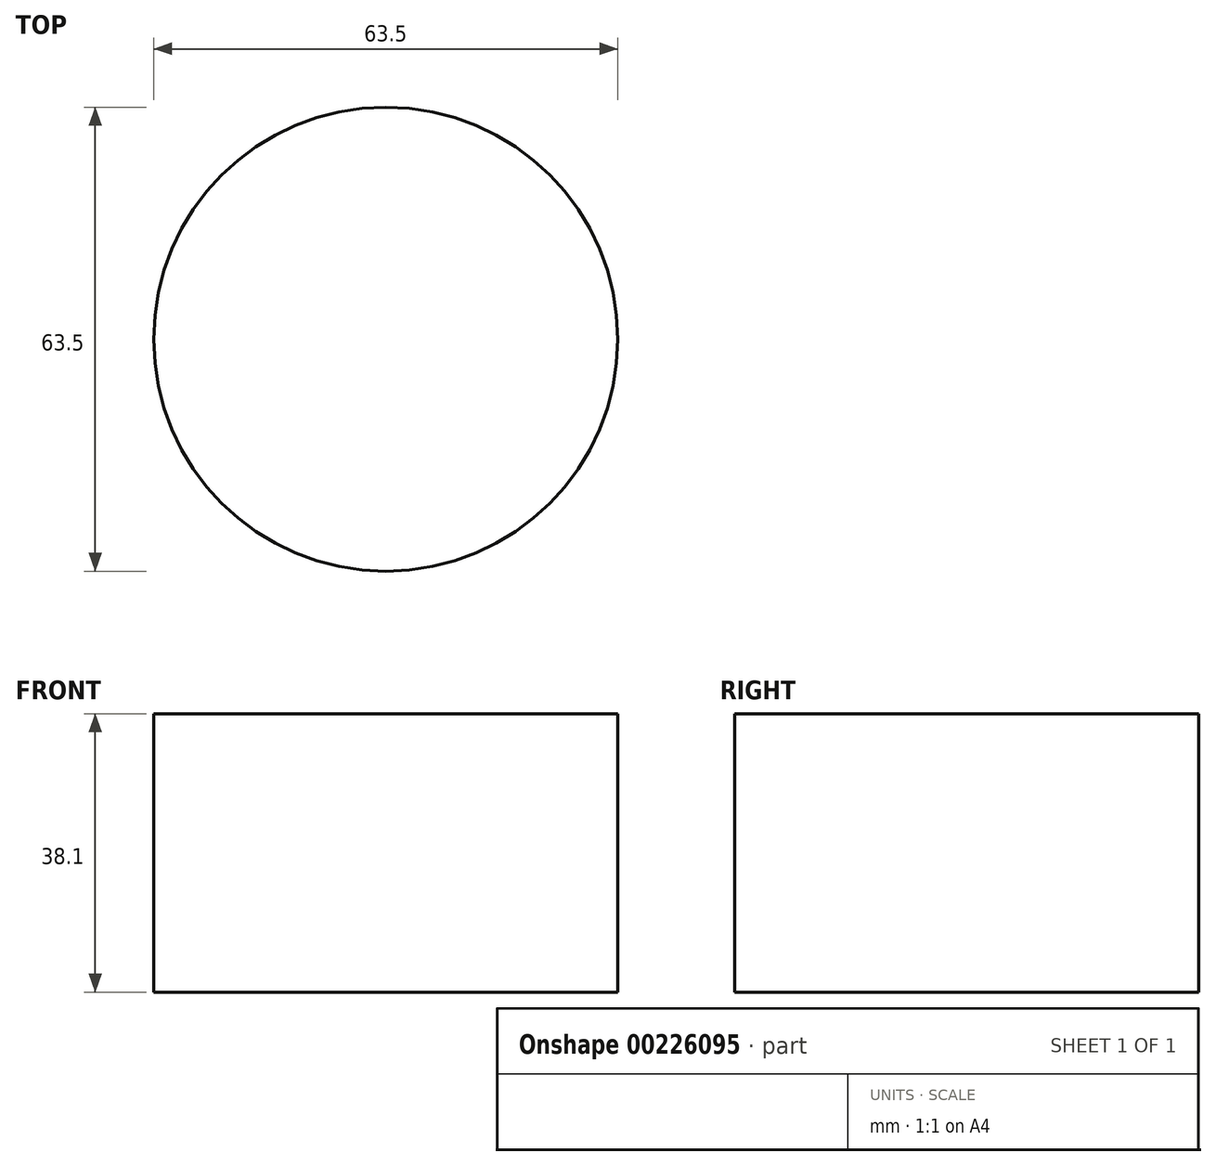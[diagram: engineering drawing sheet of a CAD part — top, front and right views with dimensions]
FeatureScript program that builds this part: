
annotation { "Feature Type Name" : "Feature", "Feature Type Description" : "" }
export const myFeature = defineFeature(function(context is Context, id is Id, definition is map)
    precondition{}
    {
        {
            var Q0;
            Q0=qCreatedBy(makeId("Top.planeOp"),FACE);
            var sketch = newSketch(context, id + "F0", { "sketchPlane" : qUnion([Q0])});
            skCircle(sketch, "E0", {"center": v(0, 0) * mm, "radius": 31.75 * mm});
            skSolve(sketch);
        }
        {
            var Q0;
            Q0=qSketchRegion(id+"F0",true);
            extrude(context, id + "F1", {"entities" : qUnion([Q0]), "depth" : 38.1 * mm});
        }
        {
            var Q0;
            Q0=qCreatedBy(makeId("Top.planeOp"),FACE);
            var sketch = newSketch(context, id + "F2", { "sketchPlane" : qUnion([Q0])});
            skCircle(sketch, "E1", {"center": v(0, 31.75) * mm, "radius": 5.08 * mm});
            skCircle(sketch, "E2.1.0", {"center": v(-18.66, 25.69) * mm, "radius": 5.08 * mm});
            skCircle(sketch, "E2.2.0", {"center": v(-30.2, 9.81) * mm, "radius": 5.08 * mm});
            skCircle(sketch, "E2.3.0", {"center": v(-30.2, -9.81) * mm, "radius": 5.08 * mm});
            skCircle(sketch, "E2.4.0", {"center": v(-18.66, -25.69) * mm, "radius": 5.08 * mm});
            skCircle(sketch, "E2.5.0", {"center": v(0, -31.75) * mm, "radius": 5.08 * mm});
            skCircle(sketch, "E2.6.0", {"center": v(18.66, -25.69) * mm, "radius": 5.08 * mm});
            skCircle(sketch, "E2.7.0", {"center": v(30.2, -9.81) * mm, "radius": 5.08 * mm});
            skCircle(sketch, "E2.8.0", {"center": v(30.2, 9.81) * mm, "radius": 5.08 * mm});
            skCircle(sketch, "E2.9.0", {"center": v(18.66, 25.69) * mm, "radius": 5.08 * mm});
            skPoint(sketch, "E2.center", {"position": v(0, 0) * mm});
            skSolve(sketch);
        }
        {
            var Q0;
            Q0=qSketchRegion(id+"F2",true);
            extrude(context, id + "F3", {"entities" : qUnion([Q0]), "depth" : 50.8 * mm});
        }
        {
            var Q0;
            Q0=makeQuery(id+"F1.opExtrude","SWEPT_BODY",BODY,{"disambiguationData":[OSD([sQuery(id+"F0.wireOp",EDGE,"E0")])]});
            var Q1;
            Q1=makeQuery(id+"F3.opExtrude","SWEPT_BODY",BODY,{"disambiguationData":[OSD([sQuery(id+"F2.wireOp",EDGE,"E1")])]});
            var Q2;
            Q2=makeQuery(id+"F3.opExtrude","SWEPT_BODY",BODY,{"disambiguationData":[OSD([sQuery(id+"F2.wireOp",EDGE,"E2.1.0")])]});
            var Q3;
            Q3=makeQuery(id+"F3.opExtrude","SWEPT_BODY",BODY,{"disambiguationData":[OSD([sQuery(id+"F2.wireOp",EDGE,"E2.2.0")])]});
            var Q4;
            Q4=makeQuery(id+"F3.opExtrude","SWEPT_BODY",BODY,{"disambiguationData":[OSD([sQuery(id+"F2.wireOp",EDGE,"E2.3.0")])]});
            var Q5;
            Q5=makeQuery(id+"F3.opExtrude","SWEPT_BODY",BODY,{"disambiguationData":[OSD([sQuery(id+"F2.wireOp",EDGE,"E2.4.0")])]});
            var Q6;
            Q6=makeQuery(id+"F3.opExtrude","SWEPT_BODY",BODY,{"disambiguationData":[OSD([sQuery(id+"F2.wireOp",EDGE,"E2.5.0")])]});
            var Q7;
            Q7=makeQuery(id+"F3.opExtrude","SWEPT_BODY",BODY,{"disambiguationData":[OSD([sQuery(id+"F2.wireOp",EDGE,"E2.6.0")])]});
            var Q8;
            Q8=makeQuery(id+"F3.opExtrude","SWEPT_BODY",BODY,{"disambiguationData":[OSD([sQuery(id+"F2.wireOp",EDGE,"E2.7.0")])]});
            var Q9;
            Q9=makeQuery(id+"F3.opExtrude","SWEPT_BODY",BODY,{"disambiguationData":[OSD([sQuery(id+"F2.wireOp",EDGE,"E2.8.0")])]});
            var Q10;
            Q10=makeQuery(id+"F3.opExtrude","SWEPT_BODY",BODY,{"disambiguationData":[OSD([sQuery(id+"F2.wireOp",EDGE,"E2.9.0")])]});
            booleanBodies(context, id + "F4", {"operationType" : BooleanOperationType.INTERSECTION, "tools" : qUnion([Q0, Q1, Q2, Q3, Q4, Q5, Q6, Q7, Q8, Q9, Q10]), "keepTools" : true});
        }
        {
            var Q0;
            Q0=makeQuery(id+"F3.opExtrude","SWEPT_BODY",BODY,{"disambiguationData":[OSD([sQuery(id+"F2.wireOp",EDGE,"E2.4.0")])]});
            var Q1;
            Q1=makeQuery(id+"F3.opExtrude","SWEPT_BODY",BODY,{"disambiguationData":[OSD([sQuery(id+"F2.wireOp",EDGE,"E2.3.0")])]});
            var Q2;
            Q2=makeQuery(id+"F3.opExtrude","SWEPT_BODY",BODY,{"disambiguationData":[OSD([sQuery(id+"F2.wireOp",EDGE,"E2.2.0")])]});
            var Q3;
            Q3=makeQuery(id+"F3.opExtrude","SWEPT_BODY",BODY,{"disambiguationData":[OSD([sQuery(id+"F2.wireOp",EDGE,"E2.1.0")])]});
            var Q4;
            Q4=makeQuery(id+"F3.opExtrude","SWEPT_BODY",BODY,{"disambiguationData":[OSD([sQuery(id+"F2.wireOp",EDGE,"E1")])]});
            var Q5;
            Q5=makeQuery(id+"F3.opExtrude","SWEPT_BODY",BODY,{"disambiguationData":[OSD([sQuery(id+"F2.wireOp",EDGE,"E2.9.0")])]});
            var Q6;
            Q6=makeQuery(id+"F3.opExtrude","SWEPT_BODY",BODY,{"disambiguationData":[OSD([sQuery(id+"F2.wireOp",EDGE,"E2.8.0")])]});
            var Q7;
            Q7=makeQuery(id+"F3.opExtrude","SWEPT_BODY",BODY,{"disambiguationData":[OSD([sQuery(id+"F2.wireOp",EDGE,"E2.7.0")])]});
            var Q8;
            Q8=makeQuery(id+"F3.opExtrude","SWEPT_BODY",BODY,{"disambiguationData":[OSD([sQuery(id+"F2.wireOp",EDGE,"E2.6.0")])]});
            var Q9;
            Q9=makeQuery(id+"F3.opExtrude","SWEPT_BODY",BODY,{"disambiguationData":[OSD([sQuery(id+"F2.wireOp",EDGE,"E2.5.0")])]});
            booleanBodies(context, id + "F5", {"operationType" : BooleanOperationType.INTERSECTION, "tools" : qUnion([Q0, Q1, Q2, Q3, Q4, Q5, Q6, Q7, Q8, Q9])});
        }
    });
